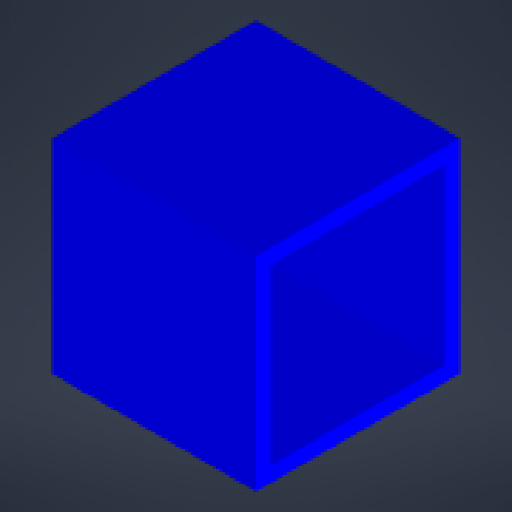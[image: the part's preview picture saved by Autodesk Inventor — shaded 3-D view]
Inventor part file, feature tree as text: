
AUTODESK INVENTOR PART (.ipt)
format: ipt  version: 2024 (Build 280153000, 153)  size: 120,320 bytes
history: native  units: mm
features: other x4, extrude x1, sketch x1, reference x1
ambient origin geometry x8: Origin, YZ Plane, XZ Plane, XY Plane, X Axis, Y Axis, Z Axis, Center Point
bodies: Body1 (feature_tree)
feature tree (7):
  other  "Твердое тело1"
  extrude  "Выдавливание1"  Depth=20.0mm
  sketch  "Эскиз1"
  reference  "Ссылка1"
  parser-record x1  (decoder bookkeeping rows leaked as tree rows — omitted from the tree; the rows remain in map.json)
  other  "base_assembly.iam"
  other  "main axis:1"
note: 1 file-system path scrubbed to <path> (originals preserved in map.json)
